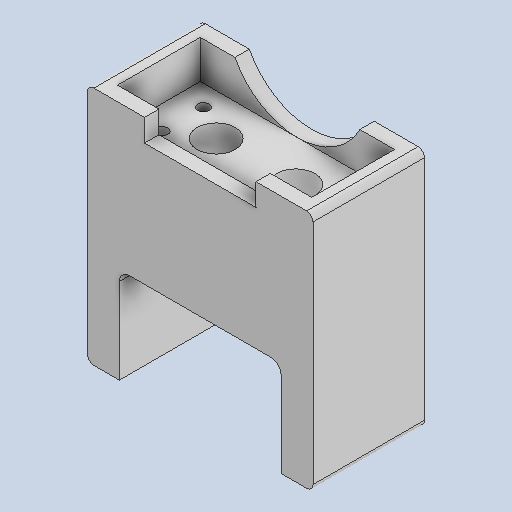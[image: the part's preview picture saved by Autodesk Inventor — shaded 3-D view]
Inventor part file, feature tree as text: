
AUTODESK INVENTOR PART (.ipt)
format: ipt  version: 2023 (Build 270158000, 158)  size: 249,856 bytes
history: native  units: in
note: dims shown in document units (in); Inventor stores cm internally (conversion verified against a paired STEP export)
features: extrude x8, sketch x7, fillet x2
ambient origin geometry x8: Origin, YZ Plane, XZ Plane, XY Plane, X Axis, Y Axis, Z Axis, Center Point
bodies: Solid1 (feature_tree)
feature tree (17):
  sketch  "Sketch1"  dims[d0=0.9843in d1=2.3622in]
  extrude  "Extrusion1"  Depth=2.3622in
  extrude  "Extrusion2"  Depth=0.0197in
  extrude  "Extrusion3"  Depth=0.0197in
  extrude  "Extrusion4"  Depth=1.811in
  extrude  "Extrusion5"  Depth=2.7874in
  extrude  "Extrusion6"  Depth=0.3937in TaperAngle=0.0deg
  fillet  "Fillet1"  Radius=0.3937in
  fillet  "Fillet2"  Radius=2.0in
  extrude  "Extrusion7"  Depth=0.125in
  extrude  "Extrusion8"  Depth=0.3937in
  sketch  "Sketch2"  dims[d2=0.0197in d3=0.0197in]
  sketch  "Sketch3"  dims[d4=0.0197in d5=0.0197in]
  sketch  "Sketch4"  dims[d6=0.1417in d7=1.811in]
  sketch  "Sketch5"  dims[d8=0.5118in d9=2.7874in]
  sketch  "Sketch6"  dims[d10=1.378in d11=0.3937in d12=0.0in]
  sketch  "Sketch7"  dims[d13=1.3937in d14=0.0in d15=0.3937in d16=0.0787in d17=0.0in d18=0.0in d19=0.3937in d20=1.1969in d21=0.0in d22=0.0in d23=2.0in d24=0.125in d25=0.3937in d26=1.1811in d27=0.3937in d28=0.0in d29=0.2362in d30=0.9843in d31=0.3937in d32=0.0in d34=0.4724in d35=0.3937in d36=0.0in d37=0.0787in d38=0.0787in d39=1.5118in d40=1.378in d41=2.0812in d42=0.0in d44=0.8661in d45=0.3937in d46=0.3937in d47=0.0in]
